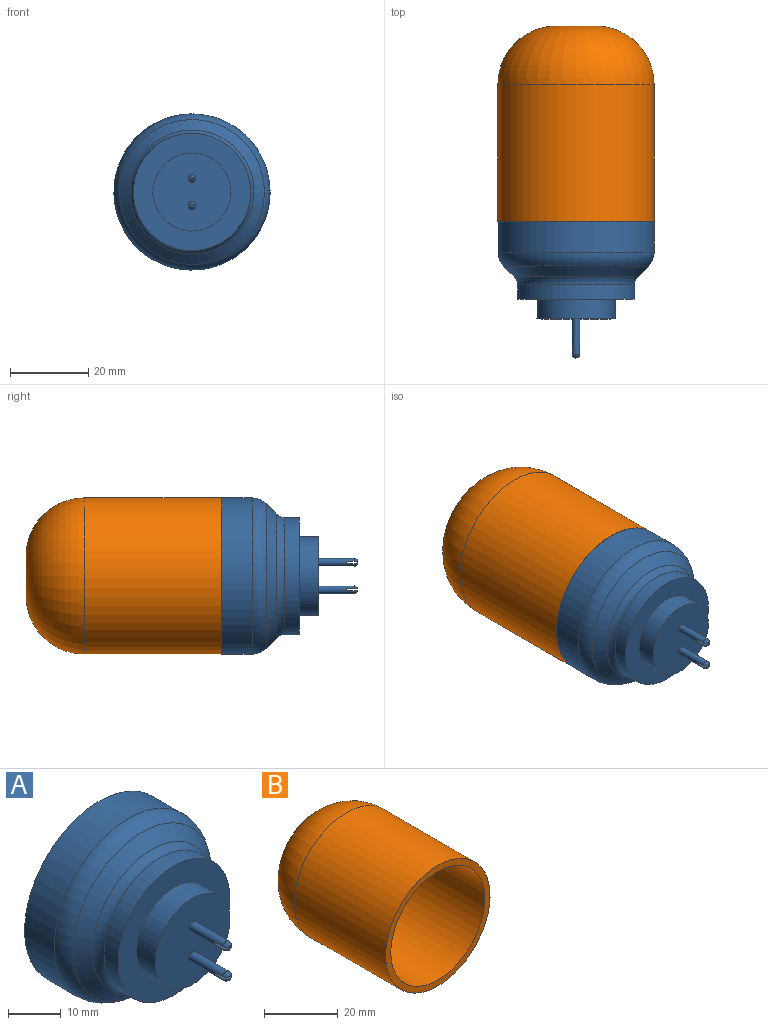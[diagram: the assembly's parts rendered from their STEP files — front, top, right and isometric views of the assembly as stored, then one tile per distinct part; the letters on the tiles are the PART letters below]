
ASSEMBLY  parts=2 mates=1
PART A: 27 faces, bbox 43.3x35x43.3 mm
  f0: plane 16x16mm, normal (0,1,0), area 201.1mm2, adj f1
  f1: cylinder r=8mm len=16mm, axis (0,-1,0), area 251.3mm2, adj f0,f2
  f2: plane 26x26mm, normal (0,1,0), area 329.9mm2, adj f1,f3
  f3: cylinder r=13mm len=26mm, axis (0,-1,0), area 312.7mm2, adj f2,f4
  f4: cone r=0mm half-angle=45deg, axis (0,1,0), area 688.6mm2, adj f3,f5
  f5: cylinder r=18mm len=36mm, axis (0,-1,0), area 1037.3mm2, adj f4,f6
  f6: plane 40x40mm, normal (0,1,0), area 238.8mm2, adj f5,f7
  f7: cylinder r=20mm len=40mm, axis (0,-1,0), area 996.4mm2, adj f6,f8
  f8: torus R=15mm, axis (0,-1,0), area 481.2mm2, adj f7,f9
  f9: cone r=0mm half-angle=45deg, axis (0,1,0), area 406.2mm2, adj f8,f10
  f10: torus R=18mm, axis (0,-1,0), area 226.5mm2, adj f9,f11
  f11: cylinder r=15mm len=30mm, axis (0,-1,0), area 354.1mm2, adj f10,f13
  f12: plane 0.61x0.6mm, normal (0,1,0), area 0.3mm2, adj f14,f15,f16
  f13: plane 30x30mm, normal (0,-1,0), area 392.7mm2, adj f11,f23
  f14: plane 3x1.91mm, normal (0,0,1), area 5.3mm2, adj f12,f15,f17,f24
  f15: sphere r=1mm, area 4.7mm2, adj f12,f14,f16,f24
  f16: plane 3x1.91mm, normal (0,0,-1), area 5.3mm2, adj f12,f15,f17,f24
  f17: plane 2x0.6mm, normal (0,-1,0), area 1.2mm2, adj f14,f16,f24
  f18: sphere r=1mm, area 2.2mm2, adj f19,f25
  f19: plane 2.95x1.91mm, normal (0,0,1), area 5.2mm2, adj f18,f22,f25
  f20: sphere r=1mm, area 2.2mm2, adj f21,f25
  f21: plane 2.95x1.91mm, normal (0,0,-1), area 5.2mm2, adj f20,f22,f25
  f22: plane 2x0.6mm, normal (0,-1,0), area 1.2mm2, adj f19,f21,f25
  f23: cylinder r=10mm len=20mm, axis (0,-1,0), area 314.2mm2, adj f13,f26
  f24: cylinder r=1mm len=9mm, axis (0,-1,0), area 54.1mm2, adj f14,f15,f16,f17,f26
  f25: cylinder r=1mm len=9mm, axis (0,-1,0), area 54.1mm2, adj f18,f19,f20,f21,f22,f26
  f26: plane 20x20mm, normal (0,-1,0), area 307.9mm2, adj f23,f24,f25
PART B: 7 faces, bbox 40x50x40 mm
  f0: plane 10x10mm, normal (0,-1,0), area 78.5mm2, adj f1
  f1: torus R=5mm, axis (0,1,0), area 1703.4mm2, adj f0,f2
  f2: cylinder r=18mm len=36mm, axis (0,1,0), area 3958.4mm2, adj f1,f3
  f3: plane 40x40mm, normal (0,-1,0), area 238.8mm2, adj f2,f4
  f4: cylinder r=20mm len=40mm, axis (0,1,0), area 4398.2mm2, adj f3,f5
  f5: torus R=5mm, axis (0,1,0), area 2153.9mm2, adj f4,f6
  f6: plane 10x10mm, normal (0,1,0), area 78.5mm2, adj f5
PLACE A t=(-6.9,40.37,38.24)mm
PLACE B t=(-6.9,90.37,38.24)mm
MATE planar A.f8 <-> B.f1  axis (0,1,0) through (-6.9,40.37,38.24)mm
